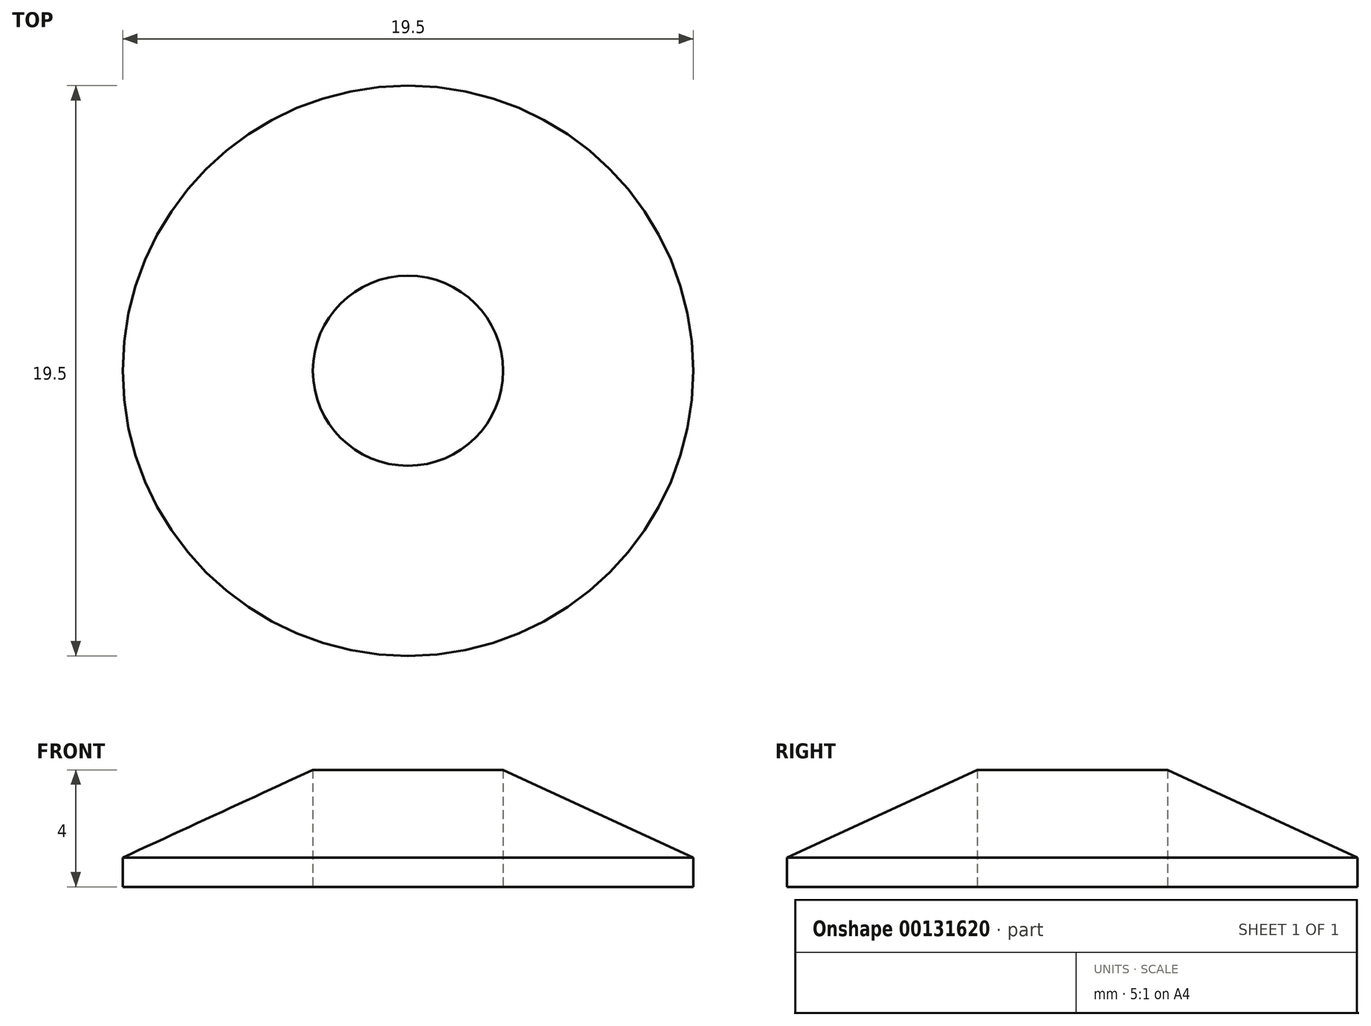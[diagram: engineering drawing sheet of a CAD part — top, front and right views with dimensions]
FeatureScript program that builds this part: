
annotation { "Feature Type Name" : "Feature", "Feature Type Description" : "" }
export const myFeature = defineFeature(function(context is Context, id is Id, definition is map)
    precondition{}
    {
        {
            var Q0;
            Q0=qCreatedBy(makeId("Front.planeOp"),FACE);
            var sketch = newSketch(context, id + "F0", { "sketchPlane" : qUnion([Q0])});
            skLineSegment(sketch, "E0", {"start": v(0, 0) * mm, "end": v(0, 2.37) * mm});
            skLineSegment(sketch, "E1", {"start": v(3.25, 0) * mm, "end": v(3.25, 4) * mm});
            skLineSegment(sketch, "E2", {"start": v(3.25, 4) * mm, "end": v(9.75, 1) * mm});
            skLineSegment(sketch, "E3", {"start": v(9.75, 1) * mm, "end": v(9.75, 0) * mm});
            skLineSegment(sketch, "E4", {"start": v(9.75, 0) * mm, "end": v(3.25, 0) * mm});
            skSolve(sketch);
        }
        {
            var Q0;
            Q0 = qSketchRegion(id + "F0", true);
            var Q1;
            Q1=sQuery(id+"F0.wireOp",EDGE,"E0");
            revolve(context, id + "F1", {"entities" : qUnion([Q0]), "axis" : qUnion([Q1]), "revolveType" : RevolveType.FULL});
        }
    });
